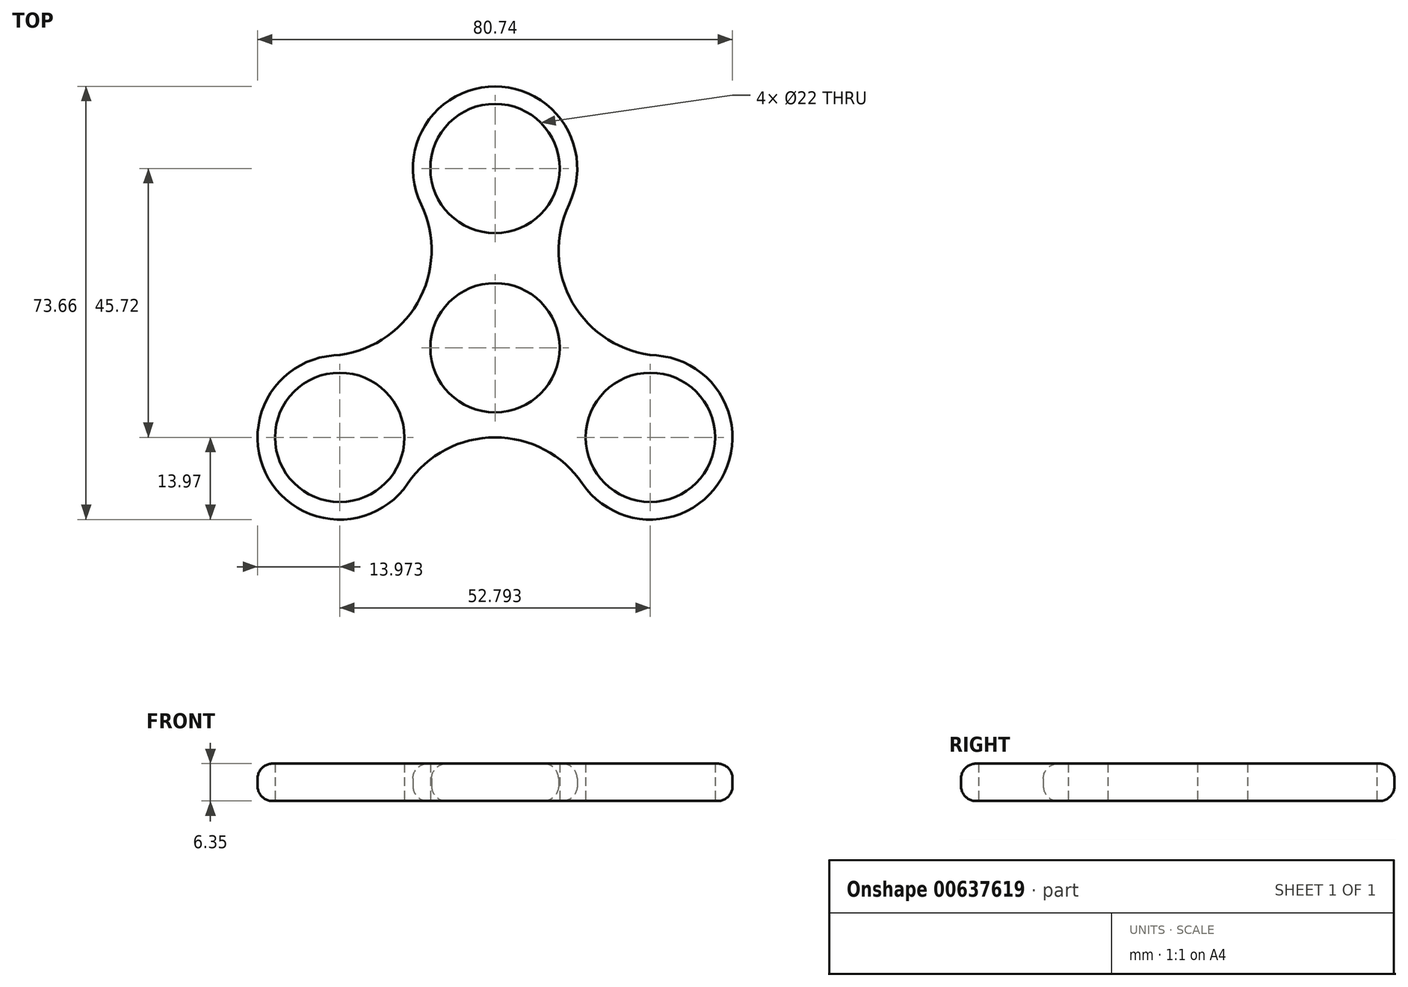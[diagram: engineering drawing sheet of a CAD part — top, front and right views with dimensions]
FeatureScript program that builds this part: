
annotation { "Feature Type Name" : "Feature", "Feature Type Description" : "" }
export const myFeature = defineFeature(function(context is Context, id is Id, definition is map)
    precondition{}
    {
        {
            var Q0;
            Q0=qCreatedBy(makeId("Top.planeOp"),FACE);
            var sketch = newSketch(context, id + "F0", { "sketchPlane" : qUnion([Q0])});
            skCircle(sketch, "E0", {"center": v(0, 0) * mm, "radius": 11 * mm});
            skCircle(sketch, "E1", {"center": v(0, 30.48) * mm, "radius": 11 * mm});
            skCircle(sketch, "E2.1.0", {"center": v(-26.4, -15.24) * mm, "radius": 11 * mm});
            skCircle(sketch, "E2.2.0", {"center": v(26.4, -15.24) * mm, "radius": 11 * mm});
            skArc(sketch, "E3", {"start": v(12.58, 24.4) * mm, "mid": v(0, 44.45) * mm, "end": v(-12.58, 24.4) * mm});
            skArc(sketch, "E4", {"start": v(-27.42, -1.3) * mm, "mid": v(-38.5, -22.22) * mm, "end": v(-14.84, -23.1) * mm});
            skArc(sketch, "E5", {"start": v(14.84, -23.1) * mm, "mid": v(38.5, -22.23) * mm, "end": v(27.42, -1.3) * mm});
            skArc(sketch, "E6", {"start": v(-27.42, -1.3) * mm, "mid": v(-13.2, 7.62) * mm, "end": v(-12.58, 24.4) * mm});
            skArc(sketch, "E7.1.0", {"start": v(14.84, -23.1) * mm, "mid": v(0, -15.23) * mm, "end": v(-14.84, -23.1) * mm});
            skArc(sketch, "E7.2.0", {"start": v(12.58, 24.4) * mm, "mid": v(13.2, 7.62) * mm, "end": v(27.42, -1.3) * mm});
            skSolve(sketch);
        }
        {
            var Q0;
            Q0=makeQuery(id+"F0.imprint","IMPRINT",FACE,{"disambiguationData":[TD([[makeQuery(id+"F0.imprint","IMPRINT",EDGE,{"derivedFrom":sQuery(id+"F0.wireOp",EDGE,"E0")}),-1.0]])]});
            extrude(context, id + "F1", {"entities" : qUnion([Q0]), "depth" : 6.35 * mm, "offsetDistance" : 25.4 * mm});
        }
        {
            var Q0;
            Q0=makeQuery(id+"F1.opExtrude","CAP_EDGE",EDGE,{"disambiguationData":[OSD([sQuery(id+"F0.wireOp",EDGE,"E7.1.0")])],"isStart":false});
            var Q1;
            Q1=makeQuery(id+"F1.opExtrude","CAP_EDGE",EDGE,{"disambiguationData":[OSD([sQuery(id+"F0.wireOp",EDGE,"E7.2.0")])],"isStart":true});
            fillet(context, id + "F2", {"entities" : qUnion([Q0, Q1]), "radius" : 2.54 * mm, "tangentPropagation" : true, "allowEdgeOverflow" : false});
        }
    });
